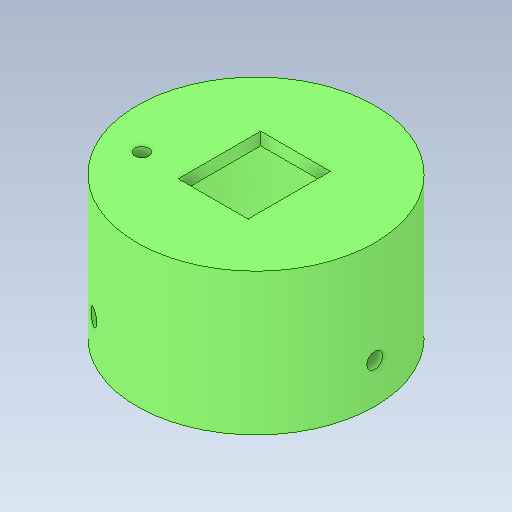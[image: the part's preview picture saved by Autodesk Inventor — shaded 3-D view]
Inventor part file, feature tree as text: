
AUTODESK INVENTOR PART (.ipt)
format: ipt  version: 2020 (Build 240168000, 168)  size: 155,648 bytes
history: native  units: in
note: dims shown in document units (in); Inventor stores cm internally (conversion verified against a paired STEP export)
features: sketch x4, extrude x3, revolve x1, pattern_circular x1
ambient origin geometry x8: Origin, YZ Plane, XZ Plane, XY Plane, X Axis, Y Axis, Z Axis, Center Point
bodies: Solid1 (feature_tree)
feature tree (9):
  revolve  "Revolution1"  [1 undecoded]
  extrude  "Extrusion2"  TaperAngle=45.0deg  [1 undecoded]
  pattern_circular  "Circular Pattern1"  Angle=90.0deg  [1 undecoded]
  extrude  "Extrusion3"  Depth=0.65in
  extrude  "Extrusion4"  Depth=0.65in
  sketch  "Sketch1"  dims[d1=0.875in d2=0.2in d4=0.1in d5=1.118in]
  sketch  "Sketch4"  dims[d6=30.0deg d7=45.0deg]
  sketch  "Sketch5"  dims[d10=0.8375in]
  sketch  "Sketch6"  dims[d13=0.1in d15=90.0deg d22=0.275in d33=0.125in d34=0.315in d35=1.0in d36=0.0in d37=1.1811in d38=360.0deg d50=0.1in d51=0.55in d52=0.65in d53=1.0in d54=0.0in d56=0.013in d57=1.0in d58=0.0in d59=0.3in d60=0.6in]
note: 3 required parameter values undecoded (feature->parameter linkage not recoverable at this tier; creation-order binding heuristic only, values carry confidence <= 0.55)